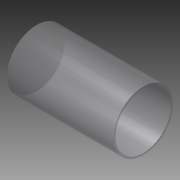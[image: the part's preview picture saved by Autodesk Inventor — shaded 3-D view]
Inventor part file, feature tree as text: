
AUTODESK INVENTOR PART (.ipt)
format: ipt  version: 2015 (Build 190159000, 159)  size: 87,552 bytes
history: native  units: mm
features: extrude x1, sketch x1
ambient origin geometry x8: Origin, YZ Plane, XZ Plane, XY Plane, X Axis, Y Axis, Z Axis, Center Point
bodies: Solid1 (feature_tree)
feature tree (2):
  extrude  "Extrusion1"  Depth=180.0mm
  sketch  "Sketch1"  dims[d0=100.0mm d2=94.0mm d3=180.0mm d4=0.0mm]
